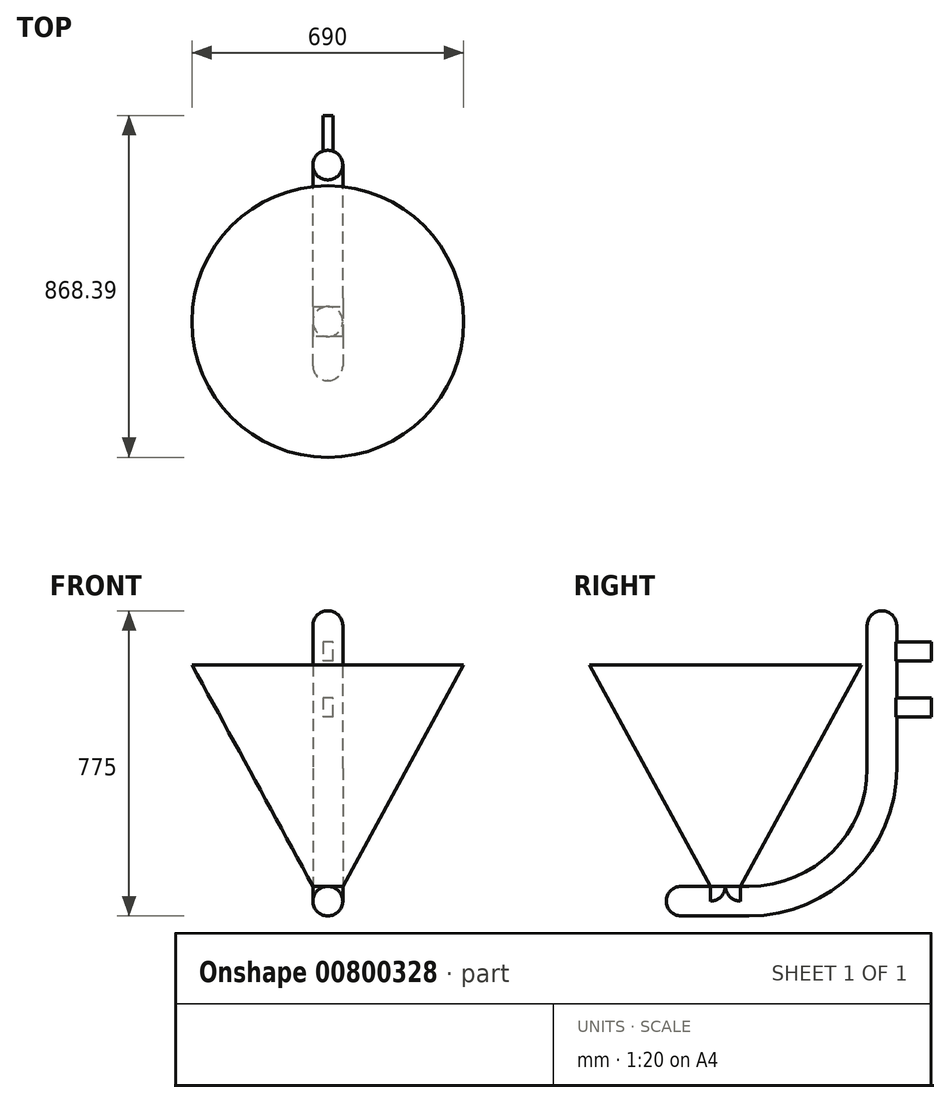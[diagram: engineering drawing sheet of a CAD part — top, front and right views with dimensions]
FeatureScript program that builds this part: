
annotation { "Feature Type Name" : "Feature", "Feature Type Description" : "" }
export const myFeature = defineFeature(function(context is Context, id is Id, definition is map)
    precondition{}
    {
        {
            var Q0;
            Q0=qCreatedBy(makeId("Right.planeOp"),FACE);
            var sketch = newSketch(context, id + "F0", { "sketchPlane" : qUnion([Q0])});
            skLineSegment(sketch, "E0", {"start": v(0, 0) * mm, "end": v(0, 563) * mm});
            skLineSegment(sketch, "E1", {"start": v(0, 563) * mm, "end": v(345, 563) * mm});
            skLineSegment(sketch, "E2", {"start": v(0, 563) * mm, "end": v(-345, 563) * mm});
            skLineSegment(sketch, "E3", {"start": v(0, 0) * mm, "end": v(38, 0) * mm});
            skLineSegment(sketch, "E4", {"start": v(38, 0) * mm, "end": v(345, 563) * mm});
            skSolve(sketch);
        }
        {
            var Q0;
            Q0=makeQuery(id+"F0.imprint","IMPRINT",FACE,{"disambiguationData":[TD([[makeQuery(id+"F0.imprint","IMPRINT",EDGE,{"derivedFrom":sQuery(id+"F0.wireOp",EDGE,"E0")}),-1.0]])]});
            var Q1;
            Q1=sQuery(id+"F0.wireOp",EDGE,"E0");
            revolve(context, id + "F1", {"surfaceOperationType" : NewSurfaceOperationType.NEW, "entities" : qUnion([Q0]), "axis" : qUnion([Q1]), "revolveType" : RevolveType.FULL});
        }
        {
            var Q0;
            Q0=qCreatedBy(makeId("Right.planeOp"),FACE);
            var sketch = newSketch(context, id + "F2", { "sketchPlane" : qUnion([Q0])});
            skLineSegment(sketch, "E5", {"start": v(345, 563) * mm, "end": v(38, 0) * mm});
            skLineSegment(sketch, "E6", {"start": v(-38, 0) * mm, "end": v(-345, 563) * mm});
            skPoint(sketch, "E7.visualSharp", {"position": v(395, 0) * mm});
            skArc(sketch, "E7.filletArc", {"start": v(60.16, 0) * mm, "mid": v(272.3, 87.87) * mm, "end": v(360.16, 300) * mm});
            skLineSegment(sketch, "E8", {"start": v(360.16, 700) * mm, "end": v(435.16, 700) * mm});
            skLineSegment(sketch, "E9", {"start": v(-150, -75) * mm, "end": v(-150, 0) * mm});
            skArc(sketch, "E10.0", {"start": v(60.16, -75) * mm, "mid": v(325.32, 34.83) * mm, "end": v(435.16, 300) * mm});
            skLineSegment(sketch, "E11", {"start": v(60.16, 0) * mm, "end": v(-150, 0) * mm});
            skLineSegment(sketch, "E12", {"start": v(360.16, 700) * mm, "end": v(360.16, 300) * mm});
            skLineSegment(sketch, "E13", {"start": v(435.16, 700) * mm, "end": v(435.16, 300) * mm});
            skLineSegment(sketch, "E14", {"start": v(60.16, -75) * mm, "end": v(-150, -75) * mm});
            skSolve(sketch);
        }
        {
            var Q0;
            {var subQ1=sQuery(id+"F2.wireOp",EDGE,"E7.filletArc");Q0=makeQuery(id+"F2.imprint","IMPRINT",FACE,{"disambiguationData":[TD([[makeQuery(id+"F2.imprint","IMPRINT",EDGE,{"derivedFrom":subQ1}),-1.0]])]});}
            extrude(context, id + "F3", {"entities" : qUnion([Q0]), "operationType" : NewBodyOperationType.ADD, "endBound" : BoundingType.SYMMETRIC, "oppositeDirection" : true, "depth" : 76 * mm, "offsetDistance" : 25.4 * mm});
        }
        {
            var Q0;
            Q0=makeQuery(id+"F3.opExtrude","CAP_FACE",FACE,{"disambiguationData":[OSD([sQuery(id+"F2.wireOp",EDGE,"E7.filletArc"),sQuery(id+"F2.wireOp",EDGE,"E8"),sQuery(id+"F2.wireOp",EDGE,"E9"),sQuery(id+"F2.wireOp",EDGE,"E10.0"),sQuery(id+"F2.wireOp",EDGE,"E11"),sQuery(id+"F2.wireOp",EDGE,"E12"),sQuery(id+"F2.wireOp",EDGE,"E13"),sQuery(id+"F2.wireOp",EDGE,"E14")])],"isStart":false});
            var Q1;
            Q1=makeQuery(id+"F3.opExtrude","CAP_FACE",FACE,{"disambiguationData":[OSD([sQuery(id+"F2.wireOp",EDGE,"E7.filletArc"),sQuery(id+"F2.wireOp",EDGE,"E8"),sQuery(id+"F2.wireOp",EDGE,"E9"),sQuery(id+"F2.wireOp",EDGE,"E10.0"),sQuery(id+"F2.wireOp",EDGE,"E11"),sQuery(id+"F2.wireOp",EDGE,"E12"),sQuery(id+"F2.wireOp",EDGE,"E13"),sQuery(id+"F2.wireOp",EDGE,"E14")])],"isStart":true});
            var Q2;
            Q2=makeQuery(id+"F3.opExtrude","SWEPT_EDGE",EDGE,{"disambiguationData":[OSD([sQuery(id+"F2.wireOp",EDGE,"E9"),sQuery(id+"F2.wireOp",EDGE,"E11")])]});
            var Q3;
            Q3=makeQuery(id+"F3.opExtrude","SWEPT_EDGE",EDGE,{"disambiguationData":[OSD([sQuery(id+"F2.wireOp",EDGE,"E9"),sQuery(id+"F2.wireOp",EDGE,"E14")])]});
            var Q4;
            Q4=makeQuery(id+"F3.opExtrude","SWEPT_EDGE",EDGE,{"disambiguationData":[OSD([sQuery(id+"F2.wireOp",EDGE,"E8"),sQuery(id+"F2.wireOp",EDGE,"E13")])]});
            var Q5;
            Q5=makeQuery(id+"F3.opExtrude","SWEPT_EDGE",EDGE,{"disambiguationData":[OSD([sQuery(id+"F2.wireOp",EDGE,"E8"),sQuery(id+"F2.wireOp",EDGE,"E12")])]});
            fillet(context, id + "F4", {"entities" : qUnion([Q0, Q1, Q2, Q3, Q4, Q5]), "radius" : 37.5 * mm, "tangentPropagation" : true, "allowEdgeOverflow" : false});
        }
        {
            var Q0;
            Q0=qCreatedBy(makeId("Right.planeOp"),FACE);
            var sketch = newSketch(context, id + "F5", { "sketchPlane" : qUnion([Q0])});
            skLineSegment(sketch, "E15.bottom", {"start": v(424.54, 621) * mm, "end": v(523.4, 621) * mm});
            skLineSegment(sketch, "E15.top", {"start": v(424.54, 572.18) * mm, "end": v(523.4, 572.18) * mm});
            skLineSegment(sketch, "E15.left", {"start": v(424.54, 621) * mm, "end": v(424.54, 572.18) * mm});
            skLineSegment(sketch, "E15.right", {"start": v(523.4, 621) * mm, "end": v(523.4, 572.18) * mm});
            skLineSegment(sketch, "E16.bottom", {"start": v(424.54, 479.28) * mm, "end": v(523.4, 479.28) * mm});
            skLineSegment(sketch, "E16.top", {"start": v(424.54, 430.45) * mm, "end": v(523.4, 430.45) * mm});
            skLineSegment(sketch, "E16.left", {"start": v(424.54, 479.28) * mm, "end": v(424.54, 430.45) * mm});
            skLineSegment(sketch, "E16.right", {"start": v(523.4, 479.28) * mm, "end": v(523.4, 430.45) * mm});
            skSolve(sketch);
        }
        {
            var Q0;
            Q0=makeQuery(id+"F5.imprint","IMPRINT",FACE,{"disambiguationData":[TD([[makeQuery(id+"F5.imprint","IMPRINT",EDGE,{"derivedFrom":sQuery(id+"F5.wireOp",EDGE,"E15.bottom")}),-1.0]])]});
            var Q1;
            Q1=makeQuery(id+"F5.imprint","IMPRINT",FACE,{"disambiguationData":[TD([[makeQuery(id+"F5.imprint","IMPRINT",EDGE,{"derivedFrom":sQuery(id+"F5.wireOp",EDGE,"E16.bottom")}),-1.0]])]});
            extrude(context, id + "F6", {"entities" : qUnion([Q0, Q1]), "operationType" : NewBodyOperationType.ADD, "endBound" : BoundingType.SYMMETRIC, "depth" : 25.4 * mm, "offsetDistance" : 25.4 * mm});
        }
    });
